# Revit family: Urinal-Wall_Mount-KOHLER-STRUKTURA-K-5888T-1.rfa-1
name_source: partatom
category: Plumbing Fixtures
revit_build: Autodesk Revit 2017 (Build: 20160225_1515(x64)
units: mm (PartAtom-declared; Revit-internal decimal feet)

## family parameters
Cut with Voids When Loaded = No
Host = Face
OmniClass Number = 23.31.21.00
Part Type = Normal
Room Calculation Point = No
Round Connector Dimension = Use Diameter
Shared = No

## types (3) — shared parameters
ADA Compliant = No
Assembly Code = D2010200
CW Connection = Yes
Cold Water Inlet = Cold Water Inlet
Date Modified = 03/23/2021
Default Elevation = 0"
Finish = Kohler-Vitreous_China-0-White
Flow Rate = 0 GPM
Flush Rate- GPF = 0 GPF
Flush Rate- LPF = 0 LPF
HW Connection = No
Height = 29 5/16"
Hot Water Inlet = Hot Water Inlet
Length = 14 3/16"
Manufacturer = KOHLER Co.
Master Format 2014 = 22 41 13.16
Master Format 2014 Name = Residential Urinals
Material = Vitreous China
Pressure = 0.00 psi
Product Documentation Link = https://files.kohler.com.cn
Product Name = STRUKTURA
Product Page URL = https://www.kohler.com.cn
URL = http://www.kohler.com.cn
Vent Connection = No
Waste Connection = Yes
Waste Water Outlet = Waste Water Outlet
WaterSense Certified = No
Width = 13 3/8"

## per-type parameters (varying)
| type | Description | Model | Type |
| Direct Current, 3L, 0-White | STRUKTURA TOUCHLESS URINAL 3L | K-5888T-0 | 1 |
| Direct Current, 0.5L, 0-White | STRUKTURA TOUCHLESS URINAL 0.5L | K-5888T-Y-0 | 2 |
| Direct Current, 1L, 0-White | STRUKTURA TOUCHLESS URINAL 1L | K-5888T-W-0 | 3 |

## geometry (parser evidence)
native form markers: Sweep x6
no freeform markers — native parametric forms only
